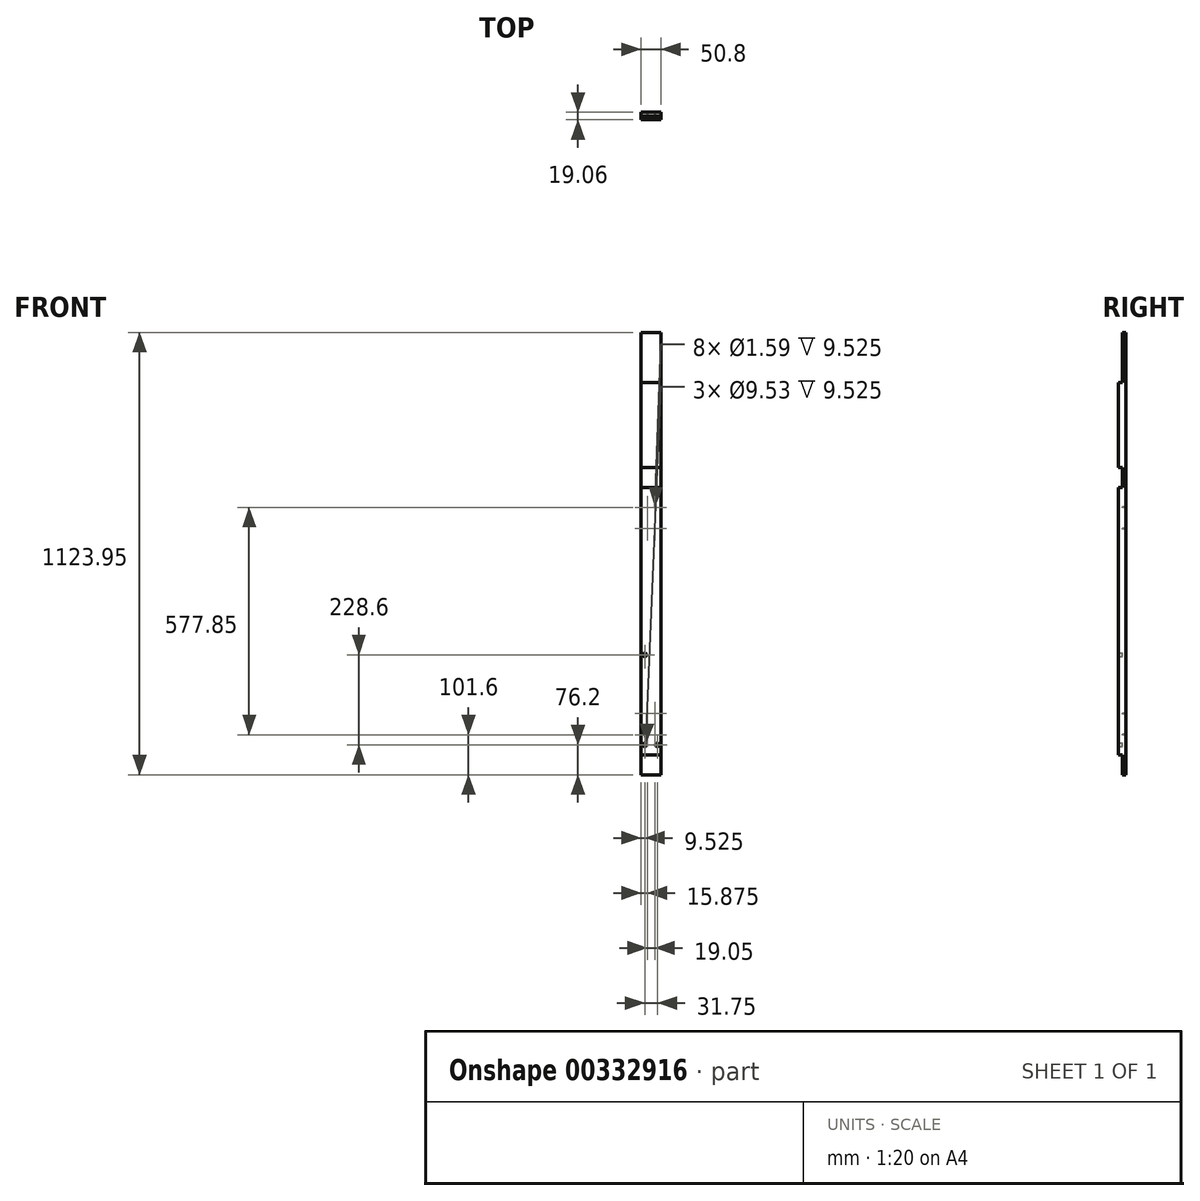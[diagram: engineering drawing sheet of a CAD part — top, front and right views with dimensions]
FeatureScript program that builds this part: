
annotation { "Feature Type Name" : "Feature", "Feature Type Description" : "" }
export const myFeature = defineFeature(function(context is Context, id is Id, definition is map)
    precondition{}
    {
        {
            var Q0;
            Q0=qCreatedBy(makeId("Top.planeOp"),FACE);
            var sketch = newSketch(context, id + "F0", { "sketchPlane" : qUnion([Q0])});
            skLineSegment(sketch, "E0.bottom", {"start": v(25.4, 9.53) * mm, "end": v(-25.4, 9.53) * mm});
            skLineSegment(sketch, "E0.top", {"start": v(25.4, -9.53) * mm, "end": v(-25.4, -9.53) * mm});
            skLineSegment(sketch, "E0.left", {"start": v(25.4, 9.53) * mm, "end": v(25.4, -9.52) * mm});
            skLineSegment(sketch, "E0.right", {"start": v(-25.4, 9.53) * mm, "end": v(-25.4, -9.53) * mm});
            skPoint(sketch, "E0.middle", {"position": v(0, 0) * mm});
            skSolve(sketch);
        }
        {
            var Q0;
            Q0=makeQuery(id+"F0.imprint","IMPRINT",FACE,{"disambiguationData":[TD([[makeQuery(id+"F0.imprint","IMPRINT",EDGE,{"derivedFrom":sQuery(id+"F0.wireOp",EDGE,"E0.bottom")}),1.0]])]});
            extrude(context, id + "F1", {"entities" : qUnion([Q0]), "depth" : 1123.95 * mm});
        }
        {
            var Q0;
            Q0=qCreatedBy(makeId("Front.planeOp"),FACE);
            var sketch = newSketch(context, id + "F2", { "sketchPlane" : qUnion([Q0])});
            skLineSegment(sketch, "E1.bottom", {"start": v(-38.77, 0) * mm, "end": v(83.66, 0) * mm});
            skLineSegment(sketch, "E1.top", {"start": v(-38.77, 50.8) * mm, "end": v(83.66, 50.8) * mm});
            skLineSegment(sketch, "E1.left", {"start": v(-38.77, 0) * mm, "end": v(-38.77, 50.8) * mm});
            skLineSegment(sketch, "E1.right", {"start": v(83.66, 0) * mm, "end": v(83.66, 50.8) * mm});
            skLineSegment(sketch, "E2.bottom", {"start": v(-44.21, 730.25) * mm, "end": v(49.65, 730.25) * mm});
            skLineSegment(sketch, "E2.top", {"start": v(-44.21, 781.05) * mm, "end": v(49.65, 781.05) * mm});
            skLineSegment(sketch, "E2.left", {"start": v(-44.21, 730.25) * mm, "end": v(-44.21, 781.05) * mm});
            skLineSegment(sketch, "E2.right", {"start": v(49.65, 730.25) * mm, "end": v(49.65, 781.05) * mm});
            skLineSegment(sketch, "E3.bottom", {"start": v(-210.36, 996.95) * mm, "end": v(132.8, 996.95) * mm});
            skLineSegment(sketch, "E3.top", {"start": v(-210.36, 1123.95) * mm, "end": v(132.8, 1123.95) * mm});
            skLineSegment(sketch, "E3.left", {"start": v(-210.36, 996.95) * mm, "end": v(-210.36, 1123.95) * mm});
            skLineSegment(sketch, "E3.right", {"start": v(132.8, 996.95) * mm, "end": v(132.8, 1123.95) * mm});
            skSolve(sketch);
        }
        {
            var Q0;
            Q0=qSketchRegion(id+"F2",true);
            extrude(context, id + "F3", {"entities" : qUnion([Q0]), "operationType" : NewBodyOperationType.REMOVE, "depth" : 25.4 * mm});
        }
        {
            var Q0;
            Q0=qCreatedBy(makeId("Front.planeOp"),FACE);
            var sketch = newSketch(context, id + "F4", { "sketchPlane" : qUnion([Q0])});
            skCircle(sketch, "E4", {"center": v(9.52, 101.6) * mm, "radius": 0.8 * mm});
            skCircle(sketch, "E5", {"center": v(9.52, 155.58) * mm, "radius": 0.8 * mm});
            skCircle(sketch, "E6", {"center": v(9.52, 625.48) * mm, "radius": 0.8 * mm});
            skCircle(sketch, "E7", {"center": v(9.52, 679.45) * mm, "radius": 0.8 * mm});
            skLineSegment(sketch, "E8", {"start": v(0, 0) * mm, "end": v(0, 1192.46) * mm, "construction": true});
            skLineSegment(sketch, "E9.bottom", {"start": v(9.52, 101.6) * mm, "end": v(-9.52, 101.6) * mm, "construction": true});
            skLineSegment(sketch, "E9.top", {"start": v(9.52, 679.45) * mm, "end": v(-9.53, 679.45) * mm, "construction": true});
            skLineSegment(sketch, "E9.left", {"start": v(9.53, 101.6) * mm, "end": v(9.52, 679.45) * mm, "construction": true});
            skLineSegment(sketch, "E9.right", {"start": v(-9.52, 101.6) * mm, "end": v(-9.53, 679.45) * mm, "construction": true});
            skCircle(sketch, "E10", {"center": v(-9.53, 625.48) * mm, "radius": 0.8 * mm});
            skCircle(sketch, "E11", {"center": v(-9.53, 679.45) * mm, "radius": 0.8 * mm});
            skCircle(sketch, "E12", {"center": v(-9.52, 101.6) * mm, "radius": 0.8 * mm});
            skCircle(sketch, "E13", {"center": v(-9.52, 155.58) * mm, "radius": 0.8 * mm});
            skSolve(sketch);
        }
        {
            var Q0;
            Q0=qSketchRegion(id+"F4",true);
            extrude(context, id + "F5", {"entities" : qUnion([Q0]), "operationType" : NewBodyOperationType.REMOVE, "oppositeDirection" : true, "depth" : 25.4 * mm});
        }
        {
            var Q0;
            Q0=qCreatedBy(makeId("Front.planeOp"),FACE);
            var sketch = newSketch(context, id + "F6", { "sketchPlane" : qUnion([Q0])});
            skCircle(sketch, "E14", {"center": v(15.88, 76.2) * mm, "radius": 4.76 * mm});
            skCircle(sketch, "E15", {"center": v(-15.88, 76.2) * mm, "radius": 4.76 * mm});
            skCircle(sketch, "E16", {"center": v(-15.88, 304.8) * mm, "radius": 4.76 * mm});
            skSolve(sketch);
        }
        {
            var Q0;
            Q0=qSketchRegion(id+"F6",true);
            extrude(context, id + "F7", {"entities" : qUnion([Q0]), "operationType" : NewBodyOperationType.REMOVE, "depth" : 25.4 * mm});
        }
    });
